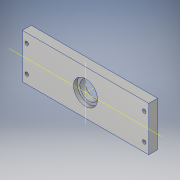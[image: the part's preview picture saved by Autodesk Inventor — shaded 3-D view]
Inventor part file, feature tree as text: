
AUTODESK INVENTOR PART (.ipt)
format: ipt  version: 2018 (Build 220112000, 112)  size: 129,024 bytes
history: native  units: mm
features: extrude x4, sketch x4, other x1
ambient origin geometry x8: Origin, YZ Plane, XZ Plane, XY Plane, X Axis, Y Axis, Z Axis, Center Point
bodies: Body1 (feature_tree)
feature tree (9):
  other  "ソリッド1"
  extrude  "押し出し1"  Depth=50.0mm
  extrude  "押し出し2"  Depth=142.0mm
  extrude  "押し出し3"  Depth=10.0mm TaperAngle=0.0deg
  extrude  "押し出し4"  Depth=27.0mm
  sketch  "スケッチ3"
  sketch  "スケッチ4"
  sketch  "スケッチ5"
  sketch  "スケッチ6"
